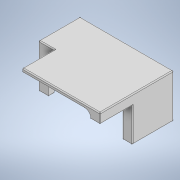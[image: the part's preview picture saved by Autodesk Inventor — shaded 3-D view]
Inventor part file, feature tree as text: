
AUTODESK INVENTOR PART (.ipt)
format: ipt  version: 2020.3 (Build 243373000, 373)  size: 266,240 bytes
history: native  units: mm
features: extrude x4, fillet x4, sketch x4
ambient origin geometry x8: Origin, YZ Plane, XZ Plane, XY Plane, X Axis, Y Axis, Z Axis, Center Point
bodies: Volumenkörper1 (feature_tree)
feature tree (12):
  extrude  "Extrusion1"  Depth=23.2mm
  extrude  "Extrusion2"  Depth=39.0mm
  fillet  "Rundung1"  Radius=5.3mm
  extrude  "Extrusion3"  Depth=24.8mm
  extrude  "Extrusion4"  Depth=0.5mm
  fillet  "Rundung2"  Radius=21.7mm
  fillet  "Rundung3"  Radius=14.5mm
  fillet  "Rundung4"  Radius=3.0mm
  sketch  "Skizze1"  dims[d0=49.6mm d1=23.2mm]
  sketch  "Skizze2"  dims[d2=2.0mm d3=39.0mm d4=5.3mm]
  sketch  "Skizze3"  dims[d5=5.3mm d6=24.8mm]
  sketch  "Skizze4"  dims[d7=22.0mm d8=0.0mm d9=43.4mm d10=21.7mm d11=14.5mm d12=0.0mm d13=3.0mm d14=10.0mm d15=2.0mm d16=2.0mm d17=2.5mm d18=42.0mm d19=21.0mm d20=46.0mm d21=23.0mm d22=10.0mm d23=0.0mm d24=5.3mm d25=17.0mm d26=0.0mm d27=3.0mm d28=0.5mm d29=0.5mm]
